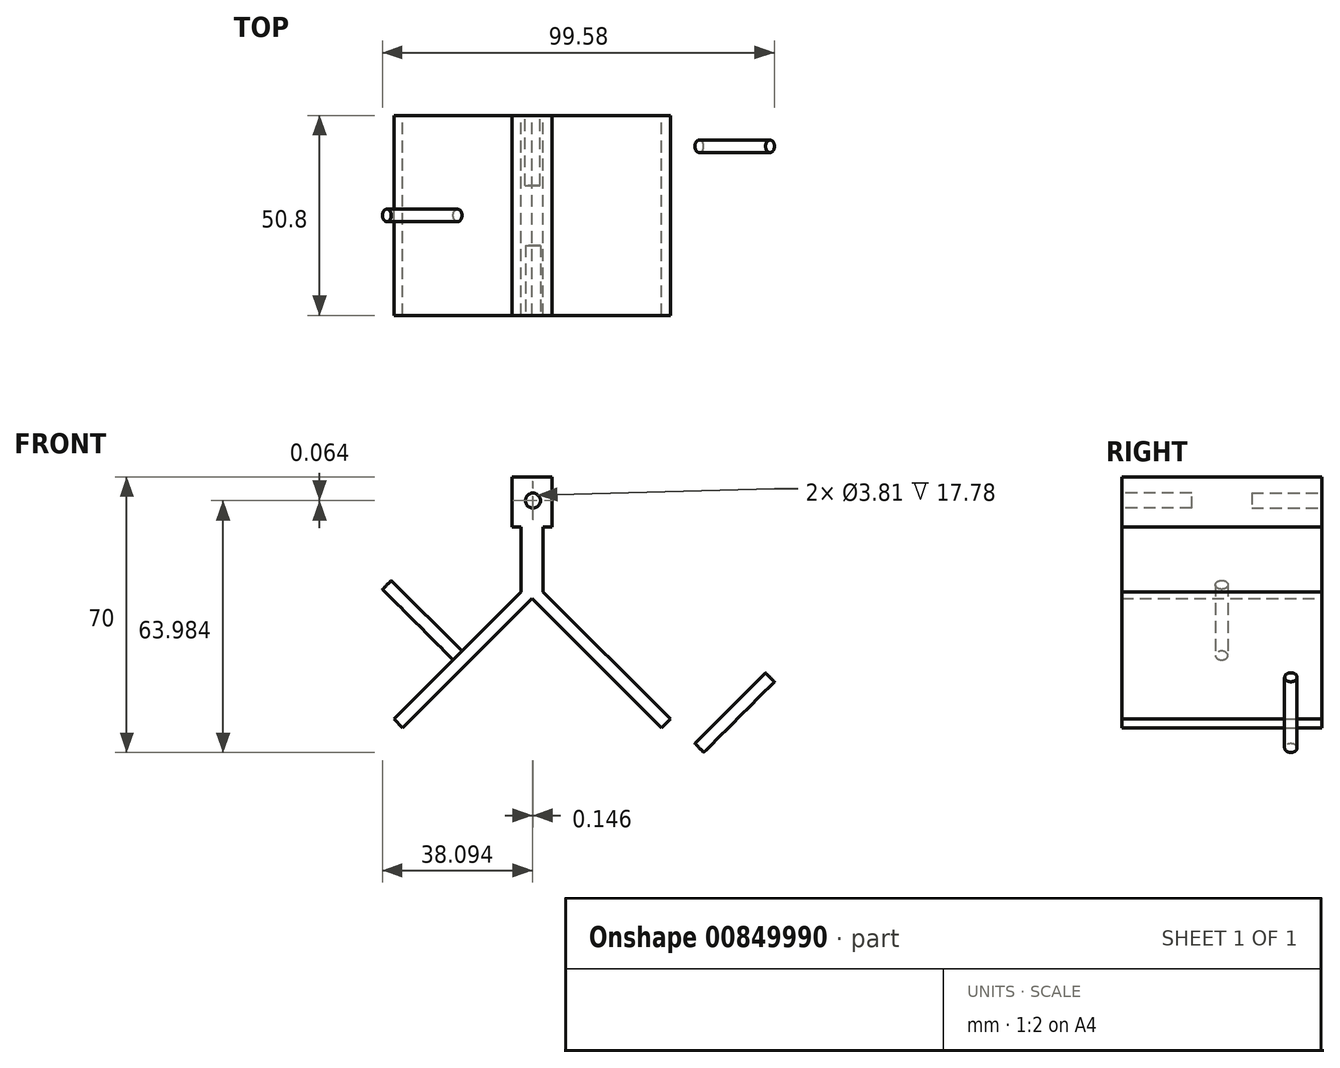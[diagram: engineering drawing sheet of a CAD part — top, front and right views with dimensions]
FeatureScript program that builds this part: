
annotation { "Feature Type Name" : "Feature", "Feature Type Description" : "" }
export const myFeature = defineFeature(function(context is Context, id is Id, definition is map)
    precondition{}
    {
        {
            var Q0;
            Q0=qCreatedBy(makeId("Front.planeOp"),FACE);
            var sketch = newSketch(context, id + "F0", { "sketchPlane" : qUnion([Q0])});
            skLineSegment(sketch, "E0", {"start": v(-19.27, 61.23) * mm, "end": v(-19.27, 48.53) * mm});
            skLineSegment(sketch, "E1", {"start": v(-19.27, 61.23) * mm, "end": v(-9.1, 61.23) * mm});
            skLineSegment(sketch, "E2", {"start": v(-9.1, 61.23) * mm, "end": v(-9.1, 48.53) * mm});
            skLineSegment(sketch, "E3", {"start": v(-19.27, 48.53) * mm, "end": v(-16.98, 48.53) * mm});
            skLineSegment(sketch, "E4", {"start": v(-9.1, 48.53) * mm, "end": v(-11.4, 48.53) * mm});
            skLineSegment(sketch, "E5", {"start": v(-16.98, 48.53) * mm, "end": v(-16.98, 32.02) * mm});
            skLineSegment(sketch, "E6", {"start": v(-11.4, 48.53) * mm, "end": v(-11.4, 32.02) * mm});
            skLineSegment(sketch, "E7", {"start": v(-11.4, 32.02) * mm, "end": v(20.93, -0.31) * mm});
            skLineSegment(sketch, "E8", {"start": v(18.69, -2.56) * mm, "end": v(-14.19, 30.32) * mm});
            skLineSegment(sketch, "E9", {"start": v(-14.19, 30.32) * mm, "end": v(-47.07, -2.56) * mm});
            skLineSegment(sketch, "E10", {"start": v(-16.98, 32.02) * mm, "end": v(-49.31, -0.31) * mm});
            skLineSegment(sketch, "E11", {"start": v(-16.98, 32.02) * mm, "end": v(-11.4, 32.02) * mm});
            skLineSegment(sketch, "E12", {"start": v(20.93, -0.31) * mm, "end": v(18.69, -2.56) * mm});
            skLineSegment(sketch, "E13", {"start": v(-14.19, 32.02) * mm, "end": v(-14.19, 30.32) * mm});
            skLineSegment(sketch, "E14", {"start": v(-49.31, -0.31) * mm, "end": v(-47.07, -2.56) * mm});
            skSolve(sketch);
        }
        {
            var Q0;
            Q0 = qSketchRegion(id + "F0", true);
            extrude(context, id + "F1", {"entities" : qUnion([Q0]), "depth" : 50.8 * mm, "offsetDistance" : 25.4 * mm});
        }
        {
            var Q0;
            Q0=makeQuery(id+"F1.opExtrude","CAP_FACE",FACE,{"disambiguationData":[OSD([sQuery(id+"F0.wireOp",EDGE,"E0"),sQuery(id+"F0.wireOp",EDGE,"E1"),sQuery(id+"F0.wireOp",EDGE,"E2"),sQuery(id+"F0.wireOp",EDGE,"E3"),sQuery(id+"F0.wireOp",EDGE,"E4"),sQuery(id+"F0.wireOp",EDGE,"E5"),sQuery(id+"F0.wireOp",EDGE,"E6"),sQuery(id+"F0.wireOp",EDGE,"E7"),sQuery(id+"F0.wireOp",EDGE,"E8"),sQuery(id+"F0.wireOp",EDGE,"E9"),sQuery(id+"F0.wireOp",EDGE,"E10"),sQuery(id+"F0.wireOp",EDGE,"E12"),sQuery(id+"F0.wireOp",EDGE,"E14")])],"isStart":true});
            var sketch = newSketch(context, id + "F2", { "sketchPlane" : qUnion([Q0])});
            skLineSegment(sketch, "E15.bottom", {"start": v(9.1, 61.23) * mm, "end": v(19.27, 61.23) * mm});
            skLineSegment(sketch, "E15.top", {"start": v(9.1, 48.53) * mm, "end": v(19.27, 48.53) * mm});
            skLineSegment(sketch, "E15.left", {"start": v(9.1, 61.23) * mm, "end": v(9.1, 48.53) * mm});
            skLineSegment(sketch, "E15.right", {"start": v(19.27, 61.23) * mm, "end": v(19.27, 48.53) * mm});
            skCircle(sketch, "E16", {"center": v(14.14, 55.28) * mm, "radius": 1.9 * mm});
            skSolve(sketch);
        }
        {
            var Q0;
            Q0=makeQuery(id+"F2.imprint","IMPRINT",FACE,{"disambiguationData":[TD([[makeQuery(id+"F2.imprint","IMPRINT",EDGE,{"derivedFrom":sQuery(id+"F2.wireOp",EDGE,"E16")}),1.0]])]});
            extrude(context, id + "F3", {"entities" : qUnion([Q0]), "operationType" : NewBodyOperationType.REMOVE, "oppositeDirection" : true, "depth" : 17.78 * mm, "offsetDistance" : 25.4 * mm});
        }
        {
            var Q0;
            Q0=makeQuery(id+"F1.opExtrude","CAP_FACE",FACE,{"disambiguationData":[OSD([sQuery(id+"F0.wireOp",EDGE,"E0"),sQuery(id+"F0.wireOp",EDGE,"E1"),sQuery(id+"F0.wireOp",EDGE,"E2"),sQuery(id+"F0.wireOp",EDGE,"E3"),sQuery(id+"F0.wireOp",EDGE,"E4"),sQuery(id+"F0.wireOp",EDGE,"E5"),sQuery(id+"F0.wireOp",EDGE,"E6"),sQuery(id+"F0.wireOp",EDGE,"E7"),sQuery(id+"F0.wireOp",EDGE,"E8"),sQuery(id+"F0.wireOp",EDGE,"E9"),sQuery(id+"F0.wireOp",EDGE,"E10"),sQuery(id+"F0.wireOp",EDGE,"E12"),sQuery(id+"F0.wireOp",EDGE,"E14")])],"isStart":false});
            var sketch = newSketch(context, id + "F4", { "sketchPlane" : qUnion([Q0])});
            skLineSegment(sketch, "E17.bottom", {"start": v(-19.27, 61.23) * mm, "end": v(-9.1, 61.23) * mm});
            skLineSegment(sketch, "E17.top", {"start": v(-19.27, 48.53) * mm, "end": v(-9.1, 48.53) * mm});
            skLineSegment(sketch, "E17.left", {"start": v(-19.27, 61.23) * mm, "end": v(-19.27, 48.53) * mm});
            skLineSegment(sketch, "E17.right", {"start": v(-9.1, 61.23) * mm, "end": v(-9.1, 48.53) * mm});
            skCircle(sketch, "E18", {"center": v(-13.99, 55.21) * mm, "radius": 1.9 * mm});
            skSolve(sketch);
        }
        {
            var Q0;
            Q0=makeQuery(id+"F1.opExtrude","SWEPT_FACE",FACE,{"disambiguationData":[OSD([sQuery(id+"F0.wireOp",EDGE,"E7")])]});
            var sketch = newSketch(context, id + "F5", { "sketchPlane" : qUnion([Q0])});
            skCircle(sketch, "E19", {"center": v(-7.84, -25.4) * mm, "radius": 1.59 * mm});
            skLineSegment(sketch, "E20.bottom", {"start": v(-30.7, -50.8) * mm, "end": v(15.02, -50.8) * mm});
            skLineSegment(sketch, "E20.top", {"start": v(-30.7, 0) * mm, "end": v(15.02, 0) * mm});
            skLineSegment(sketch, "E20.left", {"start": v(-30.7, -50.8) * mm, "end": v(-30.7, 0) * mm});
            skLineSegment(sketch, "E20.right", {"start": v(15.02, -50.8) * mm, "end": v(15.02, 0) * mm});
            skLineSegment(sketch, "E21", {"start": v(-7.84, 0) * mm, "end": v(-7.84, -50.8) * mm});
            skLineSegment(sketch, "E22", {"start": v(-30.7, -25.4) * mm, "end": v(15.02, -25.4) * mm});
            skSolve(sketch);
        }
        {
            var Q0;
            {var subQ0=sQuery(id+"F5.wireOp",EDGE,"E21");var subQ1=sQuery(id+"F5.wireOp",EDGE,"E19");var subQ2=makeQuery(id+"F5.imprint","INTERSECT",VERTEX,{"disambiguationData":[OD(0.0)],"derivedFrom":[subQ1,subQ0]});Q0=makeQuery(id+"F5.imprint","IMPRINT",FACE,{"disambiguationData":[TD([[makeQuery(id+"F5.imprint","IMPRINT",EDGE,{"disambiguationData":[TD([[subQ2,-1.0]])],"derivedFrom":subQ1}),1.0]])]});}
            var Q1;
            {var subQ0=sQuery(id+"F5.wireOp",EDGE,"E21");var subQ1=sQuery(id+"F5.wireOp",EDGE,"E19");var subQ2=makeQuery(id+"F5.imprint","INTERSECT",VERTEX,{"disambiguationData":[OD(0.0)],"derivedFrom":[subQ1,subQ0]});Q1=makeQuery(id+"F5.imprint","IMPRINT",FACE,{"disambiguationData":[TD([[makeQuery(id+"F5.imprint","IMPRINT",EDGE,{"disambiguationData":[TD([[subQ2,1.0]])],"derivedFrom":subQ1}),1.0]])]});}
            var Q2;
            {var subQ0=sQuery(id+"F5.wireOp",EDGE,"E22");var subQ1=sQuery(id+"F5.wireOp",EDGE,"E19");var subQ2=makeQuery(id+"F5.imprint","INTERSECT",VERTEX,{"disambiguationData":[OD(1.0)],"derivedFrom":[subQ1,subQ0]});Q2=makeQuery(id+"F5.imprint","IMPRINT",FACE,{"disambiguationData":[TD([[makeQuery(id+"F5.imprint","IMPRINT",EDGE,{"disambiguationData":[TD([[subQ2,-1.0]])],"derivedFrom":subQ1}),1.0]])]});}
            var Q3;
            {var subQ0=sQuery(id+"F5.wireOp",EDGE,"E22");var subQ1=sQuery(id+"F5.wireOp",EDGE,"E19");var subQ2=makeQuery(id+"F5.imprint","INTERSECT",VERTEX,{"disambiguationData":[OD(0.0)],"derivedFrom":[subQ1,subQ0]});Q3=makeQuery(id+"F5.imprint","IMPRINT",FACE,{"disambiguationData":[TD([[makeQuery(id+"F5.imprint","IMPRINT",EDGE,{"disambiguationData":[TD([[subQ2,1.0]])],"derivedFrom":subQ1}),1.0]])]});}
            extrude(context, id + "F6", {"entities" : qUnion([Q0, Q1, Q2, Q3]), "operationType" : NewBodyOperationType.ADD, "depth" : 25.4 * mm, "offsetDistance" : 25.4 * mm});
        }
        {
            var Q0;
            Q0=makeQuery(id+"F1.opExtrude","SWEPT_FACE",FACE,{"disambiguationData":[OSD([sQuery(id+"F0.wireOp",EDGE,"E10")])]});
            var sketch = newSketch(context, id + "F7", { "sketchPlane" : qUnion([Q0])});
            skLineSegment(sketch, "E23.bottom", {"start": v(0, 10.63) * mm, "end": v(50.8, 10.63) * mm});
            skLineSegment(sketch, "E23.top", {"start": v(0, -35.1) * mm, "end": v(50.8, -35.1) * mm});
            skLineSegment(sketch, "E23.left", {"start": v(0, 10.63) * mm, "end": v(0, -35.1) * mm});
            skLineSegment(sketch, "E23.right", {"start": v(50.8, 10.63) * mm, "end": v(50.8, -35.1) * mm});
            skLineSegment(sketch, "E24", {"start": v(25.4, 10.63) * mm, "end": v(25.4, -35.1) * mm});
            skLineSegment(sketch, "E25", {"start": v(0, -12.23) * mm, "end": v(50.8, -12.23) * mm});
            skCircle(sketch, "E26", {"center": v(25.4, -12.23) * mm, "radius": 1.59 * mm});
            skSolve(sketch);
        }
        {
            var Q0;
            {var subQ0=sQuery(id+"F7.wireOp",EDGE,"E26");var subQ1=sQuery(id+"F7.wireOp",EDGE,"E24");var subQ2=makeQuery(id+"F7.imprint","INTERSECT",VERTEX,{"disambiguationData":[OD(0.0)],"derivedFrom":[subQ1,subQ0]});Q0=makeQuery(id+"F7.imprint","IMPRINT",FACE,{"disambiguationData":[TD([[makeQuery(id+"F7.imprint","IMPRINT",EDGE,{"disambiguationData":[TD([[subQ2,-1.0]])],"derivedFrom":subQ1}),1.0]])]});}
            var Q1;
            {var subQ0=sQuery(id+"F7.wireOp",EDGE,"E25");var subQ1=sQuery(id+"F7.wireOp",EDGE,"E24");var subQ2=makeQuery(id+"F7.imprint","INTERSECT",VERTEX,{"derivedFrom":[subQ1,subQ0]});Q1=makeQuery(id+"F7.imprint","IMPRINT",FACE,{"disambiguationData":[TD([[makeQuery(id+"F7.imprint","IMPRINT",EDGE,{"disambiguationData":[TD([[subQ2,-1.0]])],"derivedFrom":subQ1}),1.0]])]});}
            var Q2;
            {var subQ0=sQuery(id+"F7.wireOp",EDGE,"E25");var subQ1=sQuery(id+"F7.wireOp",EDGE,"E24");var subQ2=makeQuery(id+"F7.imprint","INTERSECT",VERTEX,{"derivedFrom":[subQ1,subQ0]});Q2=makeQuery(id+"F7.imprint","IMPRINT",FACE,{"disambiguationData":[TD([[makeQuery(id+"F7.imprint","IMPRINT",EDGE,{"disambiguationData":[TD([[subQ2,-1.0]])],"derivedFrom":subQ1}),-1.0]])]});}
            var Q3;
            {var subQ0=sQuery(id+"F7.wireOp",EDGE,"E26");var subQ1=sQuery(id+"F7.wireOp",EDGE,"E24");var subQ2=makeQuery(id+"F7.imprint","INTERSECT",VERTEX,{"disambiguationData":[OD(0.0)],"derivedFrom":[subQ1,subQ0]});Q3=makeQuery(id+"F7.imprint","IMPRINT",FACE,{"disambiguationData":[TD([[makeQuery(id+"F7.imprint","IMPRINT",EDGE,{"disambiguationData":[TD([[subQ2,-1.0]])],"derivedFrom":subQ1}),-1.0]])]});}
            extrude(context, id + "F8", {"entities" : qUnion([Q0, Q1, Q2, Q3]), "operationType" : NewBodyOperationType.ADD, "depth" : 25.4 * mm, "offsetDistance" : 25.4 * mm});
        }
        {
            var Q0;
            Q0=makeQuery(id+"F4.imprint","IMPRINT",FACE,{"disambiguationData":[TD([[makeQuery(id+"F4.imprint","IMPRINT",EDGE,{"derivedFrom":sQuery(id+"F4.wireOp",EDGE,"E18")}),1.0]])]});
            extrude(context, id + "F9", {"entities" : qUnion([Q0]), "operationType" : NewBodyOperationType.REMOVE, "oppositeDirection" : true, "depth" : 17.78 * mm, "offsetDistance" : 25.4 * mm});
        }
    });
